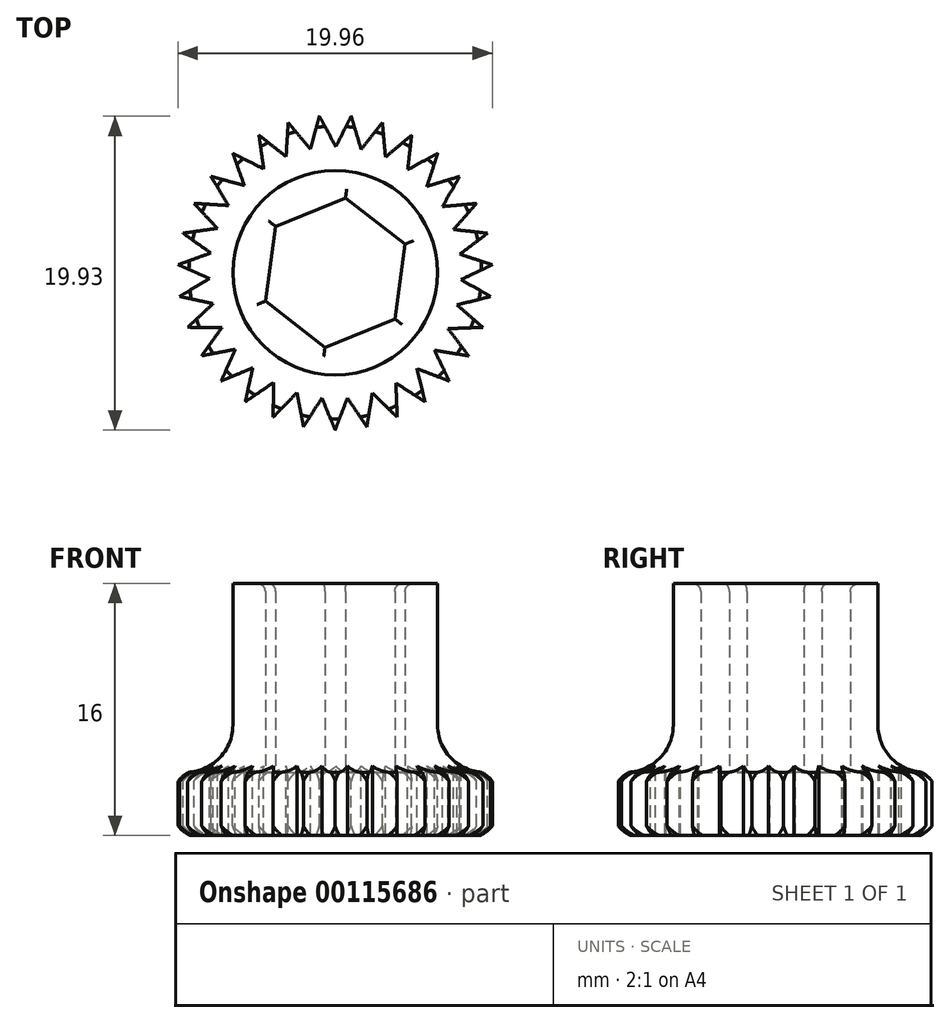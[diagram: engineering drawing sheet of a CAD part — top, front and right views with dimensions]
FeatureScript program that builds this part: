
annotation { "Feature Type Name" : "Feature", "Feature Type Description" : "" }
export const myFeature = defineFeature(function(context is Context, id is Id, definition is map)
    precondition{}
    {
        {
            var Q0;
            Q0=qCreatedBy(makeId("Top.planeOp"),FACE);
            var sketch = newSketch(context, id + "F0", { "sketchPlane" : qUnion([Q0])});
            skCircle(sketch, "E0.cCircle", {"center": v(0, 0) * mm, "radius": 4.15 * mm, "construction": true});
            skLineSegment(sketch, "E0.0", {"start": v(0.65, 4.75) * mm, "end": v(4.44, 1.81) * mm});
            skLineSegment(sketch, "E0.1", {"start": v(4.44, 1.81) * mm, "end": v(3.79, -2.94) * mm});
            skLineSegment(sketch, "E0.2", {"start": v(3.79, -2.94) * mm, "end": v(-0.65, -4.75) * mm});
            skLineSegment(sketch, "E0.3", {"start": v(-0.65, -4.75) * mm, "end": v(-4.44, -1.81) * mm});
            skLineSegment(sketch, "E0.4", {"start": v(-4.44, -1.81) * mm, "end": v(-3.79, 2.94) * mm});
            skLineSegment(sketch, "E0.5", {"start": v(-3.79, 2.94) * mm, "end": v(0.65, 4.75) * mm});
            skPoint(sketch, "E0.0.midPoint", {"position": v(2.54, 3.28) * mm});
            skCircle(sketch, "E1", {"center": v(0, 0) * mm, "radius": 6.5 * mm});
            skSolve(sketch);
        }
        {
            var Q0;
            Q0 = qSketchRegion(id + "F0", true);
            extrude(context, id + "F1", {"entities" : qUnion([Q0]), "depth" : 12 * mm});
        }
        {
            var Q0;
            Q0=makeQuery(id+"F1.opExtrude","CAP_FACE",FACE,{"disambiguationData":[OSD([sQuery(id+"F0.wireOp",EDGE,"E0.0"),sQuery(id+"F0.wireOp",EDGE,"E0.1"),sQuery(id+"F0.wireOp",EDGE,"E0.2"),sQuery(id+"F0.wireOp",EDGE,"E0.3"),sQuery(id+"F0.wireOp",EDGE,"E0.4"),sQuery(id+"F0.wireOp",EDGE,"E0.5"),sQuery(id+"F0.wireOp",EDGE,"E1")])],"isStart":true});
            var sketch = newSketch(context, id + "F2", { "sketchPlane" : qUnion([Q0])});
            skLineSegment(sketch, "E2", {"start": v(0, 0) * mm, "end": v(0, 8.68) * mm, "construction": true});
            skCircle(sketch, "E3", {"center": v(0, 0) * mm, "radius": 10 * mm, "construction": true});
            skCircle(sketch, "E4", {"center": v(0, 0) * mm, "radius": 8 * mm, "construction": true});
            skLineSegment(sketch, "E5", {"start": v(0, 10) * mm, "end": v(-0.85, 7.96) * mm});
            skLineSegment(sketch, "E6", {"start": v(-0.85, 7.96) * mm, "end": v(-2.02, 9.8) * mm});
            skLineSegment(sketch, "E7.1.0", {"start": v(-2.01, 9.8) * mm, "end": v(-2.43, 7.62) * mm});
            skLineSegment(sketch, "E7.1.1", {"start": v(-2.43, 7.62) * mm, "end": v(-3.95, 9.19) * mm});
            skLineSegment(sketch, "E7.2.0", {"start": v(-3.94, 9.19) * mm, "end": v(-3.92, 6.98) * mm});
            skLineSegment(sketch, "E7.2.1", {"start": v(-3.92, 6.98) * mm, "end": v(-5.72, 8.2) * mm});
            skLineSegment(sketch, "E7.3.0", {"start": v(-5.71, 8.2) * mm, "end": v(-5.24, 6.05) * mm});
            skLineSegment(sketch, "E7.3.1", {"start": v(-5.24, 6.05) * mm, "end": v(-7.25, 6.89) * mm});
            skLineSegment(sketch, "E7.4.0", {"start": v(-7.25, 6.89) * mm, "end": v(-6.35, 4.87) * mm});
            skLineSegment(sketch, "E7.4.1", {"start": v(-6.35, 4.87) * mm, "end": v(-8.49, 5.28) * mm});
            skLineSegment(sketch, "E7.5.0", {"start": v(-8.49, 5.29) * mm, "end": v(-7.2, 3.49) * mm});
            skLineSegment(sketch, "E7.5.1", {"start": v(-7.2, 3.49) * mm, "end": v(-9.38, 3.47) * mm});
            skLineSegment(sketch, "E7.6.0", {"start": v(-9.38, 3.47) * mm, "end": v(-7.75, 1.97) * mm});
            skLineSegment(sketch, "E7.6.1", {"start": v(-7.75, 1.97) * mm, "end": v(-9.89, 1.5) * mm});
            skLineSegment(sketch, "E7.7.0", {"start": v(-9.88, 1.51) * mm, "end": v(-8, 0.37) * mm});
            skLineSegment(sketch, "E7.7.1", {"start": v(-8, 0.37) * mm, "end": v(-9.99, -0.51) * mm});
            skLineSegment(sketch, "E7.8.0", {"start": v(-9.99, -0.5) * mm, "end": v(-7.9, -1.25) * mm});
            skLineSegment(sketch, "E7.8.1", {"start": v(-7.9, -1.25) * mm, "end": v(-9.68, -2.51) * mm});
            skLineSegment(sketch, "E7.9.0", {"start": v(-9.68, -2.5) * mm, "end": v(-7.49, -2.81) * mm});
            skLineSegment(sketch, "E7.9.1", {"start": v(-7.49, -2.81) * mm, "end": v(-8.98, -4.4) * mm});
            skLineSegment(sketch, "E7.10.0", {"start": v(-8.98, -4.4) * mm, "end": v(-6.77, -4.26) * mm});
            skLineSegment(sketch, "E7.10.1", {"start": v(-6.77, -4.26) * mm, "end": v(-7.9, -6.13) * mm});
            skLineSegment(sketch, "E7.11.0", {"start": v(-7.9, -6.12) * mm, "end": v(-5.77, -5.54) * mm});
            skLineSegment(sketch, "E7.11.1", {"start": v(-5.77, -5.54) * mm, "end": v(-6.5, -7.6) * mm});
            skLineSegment(sketch, "E7.12.0", {"start": v(-6.51, -7.59) * mm, "end": v(-4.54, -6.59) * mm});
            skLineSegment(sketch, "E7.12.1", {"start": v(-4.54, -6.59) * mm, "end": v(-4.85, -8.75) * mm});
            skLineSegment(sketch, "E7.13.0", {"start": v(-4.85, -8.74) * mm, "end": v(-3.12, -7.37) * mm});
            skLineSegment(sketch, "E7.13.1", {"start": v(-3.12, -7.37) * mm, "end": v(-2.99, -9.54) * mm});
            skLineSegment(sketch, "E7.14.0", {"start": v(-3, -9.54) * mm, "end": v(-1.57, -7.84) * mm});
            skLineSegment(sketch, "E7.14.1", {"start": v(-1.57, -7.84) * mm, "end": v(-1, -9.95) * mm});
            skLineSegment(sketch, "E7.15.0", {"start": v(-1.01, -9.95) * mm, "end": v(0.04, -8) * mm});
            skLineSegment(sketch, "E7.15.1", {"start": v(0.04, -8) * mm, "end": v(1.02, -9.95) * mm});
            skLineSegment(sketch, "E7.16.0", {"start": v(1.01, -9.95) * mm, "end": v(1.65, -7.83) * mm});
            skLineSegment(sketch, "E7.16.1", {"start": v(1.65, -7.83) * mm, "end": v(3, -9.54) * mm});
            skLineSegment(sketch, "E7.17.0", {"start": v(3, -9.54) * mm, "end": v(3.19, -7.34) * mm});
            skLineSegment(sketch, "E7.17.1", {"start": v(3.19, -7.34) * mm, "end": v(4.86, -8.74) * mm});
            skLineSegment(sketch, "E7.18.0", {"start": v(4.85, -8.74) * mm, "end": v(4.6, -6.54) * mm});
            skLineSegment(sketch, "E7.18.1", {"start": v(4.6, -6.54) * mm, "end": v(6.52, -7.58) * mm});
            skLineSegment(sketch, "E7.19.0", {"start": v(6.51, -7.59) * mm, "end": v(5.82, -5.48) * mm});
            skLineSegment(sketch, "E7.19.1", {"start": v(5.82, -5.48) * mm, "end": v(7.91, -6.12) * mm});
            skLineSegment(sketch, "E7.20.0", {"start": v(7.9, -6.12) * mm, "end": v(6.8, -4.2) * mm});
            skLineSegment(sketch, "E7.20.1", {"start": v(6.8, -4.2) * mm, "end": v(8.98, -4.4) * mm});
            skLineSegment(sketch, "E7.21.0", {"start": v(8.98, -4.4) * mm, "end": v(7.52, -2.74) * mm});
            skLineSegment(sketch, "E7.21.1", {"start": v(7.52, -2.74) * mm, "end": v(9.68, -2.5) * mm});
            skLineSegment(sketch, "E7.22.0", {"start": v(9.68, -2.5) * mm, "end": v(7.91, -1.17) * mm});
            skLineSegment(sketch, "E7.22.1", {"start": v(7.91, -1.17) * mm, "end": v(9.99, -0.5) * mm});
            skLineSegment(sketch, "E7.23.0", {"start": v(9.99, -0.5) * mm, "end": v(7.99, 0.44) * mm});
            skLineSegment(sketch, "E7.23.1", {"start": v(7.99, 0.44) * mm, "end": v(9.88, 1.52) * mm});
            skLineSegment(sketch, "E7.24.0", {"start": v(9.88, 1.51) * mm, "end": v(7.74, 2.04) * mm});
            skLineSegment(sketch, "E7.24.1", {"start": v(7.74, 2.04) * mm, "end": v(9.38, 3.48) * mm});
            skLineSegment(sketch, "E8.2.25.0", {"start": v(9.38, 3.47) * mm, "end": v(7.17, 3.56) * mm});
            skLineSegment(sketch, "E8.3.25.0", {"start": v(7.17, 3.56) * mm, "end": v(8.48, 5.3) * mm});
            skLineSegment(sketch, "E9.2.26.0", {"start": v(8.49, 5.29) * mm, "end": v(6.3, 4.93) * mm});
            skLineSegment(sketch, "E9.3.26.0", {"start": v(6.3, 4.93) * mm, "end": v(7.24, 6.9) * mm});
            skLineSegment(sketch, "E9.2.27.0", {"start": v(7.25, 6.89) * mm, "end": v(5.18, 6.1) * mm});
            skLineSegment(sketch, "E9.3.27.0", {"start": v(5.18, 6.1) * mm, "end": v(5.7, 8.21) * mm});
            skLineSegment(sketch, "E9.2.28.0", {"start": v(5.71, 8.2) * mm, "end": v(3.85, 7.01) * mm});
            skLineSegment(sketch, "E9.3.28.0", {"start": v(3.85, 7.01) * mm, "end": v(3.94, 9.2) * mm});
            skLineSegment(sketch, "E10.2.29.0", {"start": v(3.94, 9.19) * mm, "end": v(2.36, 7.64) * mm});
            skLineSegment(sketch, "E10.3.29.0", {"start": v(2.36, 7.64) * mm, "end": v(2, 9.8) * mm});
            skLineSegment(sketch, "E10.2.30.0", {"start": v(2.01, 9.8) * mm, "end": v(0.77, 7.96) * mm});
            skLineSegment(sketch, "E10.3.30.0", {"start": v(0.77, 7.96) * mm, "end": v(0, 10) * mm});
            skSolve(sketch);
        }
        {
            var Q0;
            Q0 = qSketchRegion(id + "F2", true);
            extrude(context, id + "F3", {"entities" : qUnion([Q0]), "operationType" : NewBodyOperationType.ADD, "depth" : 4 * mm});
        }
        {
            var Q0;
            Q0=makeQuery(id+"F1.opExtrude","CAP_EDGE",EDGE,{"disambiguationData":[OSD([sQuery(id+"F0.wireOp",EDGE,"E1")])],"isStart":true});
            fillet(context, id + "F4", {"entities" : qUnion([Q0]), "radius" : 3 * mm, "tangentPropagation" : true, "allowEdgeOverflow" : false});
        }
        {
            var Q0;
            Q0=qCreatedBy(makeId("Right.planeOp"),FACE);
            var sketch = newSketch(context, id + "F5", { "sketchPlane" : qUnion([Q0])});
            skPoint(sketch, "E11.0", {"position": v(2.5, -4) * mm});
            skLineSegment(sketch, "E12", {"start": v(0, -4) * mm, "end": v(-4.72, -4) * mm});
            skLineSegment(sketch, "E13", {"start": v(-10, -4) * mm, "end": v(-10, 0.3) * mm});
            skLineSegment(sketch, "E14", {"start": v(-10, 0.3) * mm, "end": v(-12.39, -5.28) * mm});
            skLineSegment(sketch, "E15", {"start": v(-12.39, -5.28) * mm, "end": v(0, -4.92) * mm});
            skArc(sketch, "E16", {"start": v(-8.86, 0.19) * mm, "mid": v(-10.44, -2.42) * mm, "end": v(-7.99, -4.23) * mm});
            skLineSegment(sketch, "E17", {"start": v(-7.99, -4.23) * mm, "end": v(-4.72, -4) * mm});
            skLineSegment(sketch, "E18", {"start": v(-8.86, 0.19) * mm, "end": v(-10, 0.3) * mm});
            skLineSegment(sketch, "E19.trimOffspring", {"start": v(-9.24, -4) * mm, "end": v(-10, -4) * mm});
            skLineSegment(sketch, "E20", {"start": v(0, -5.6) * mm, "end": v(0, 3.11) * mm, "construction": true});
            skLineSegment(sketch, "E21", {"start": v(0, -4.92) * mm, "end": v(0, -4) * mm});
            skSolve(sketch);
        }
        {
            var Q0;
            Q0 = qSketchRegion(id + "F5", true);
            var Q1;
            Q1=sQuery(id+"F5.wireOp",EDGE,"E20");
            revolve(context, id + "F6", {"operationType" : NewBodyOperationType.REMOVE, "entities" : qUnion([Q0]), "axis" : qUnion([Q1]), "revolveType" : RevolveType.FULL, "oppositeDirection" : true});
        }
        {
            var Q0;
            Q0=makeQuery(id+"F1.opExtrude","CAP_EDGE",EDGE,{"disambiguationData":[OSD([sQuery(id+"F0.wireOp",EDGE,"E0.1")])],"isStart":false});
            var Q1;
            Q1=makeQuery(id+"F1.opExtrude","CAP_EDGE",EDGE,{"disambiguationData":[OSD([sQuery(id+"F0.wireOp",EDGE,"E0.0")])],"isStart":false});
            var Q2;
            Q2=makeQuery(id+"F1.opExtrude","CAP_EDGE",EDGE,{"disambiguationData":[OSD([sQuery(id+"F0.wireOp",EDGE,"E0.5")])],"isStart":false});
            var Q3;
            Q3=makeQuery(id+"F1.opExtrude","CAP_EDGE",EDGE,{"disambiguationData":[OSD([sQuery(id+"F0.wireOp",EDGE,"E0.4")])],"isStart":false});
            var Q4;
            Q4=makeQuery(id+"F1.opExtrude","CAP_EDGE",EDGE,{"disambiguationData":[OSD([sQuery(id+"F0.wireOp",EDGE,"E0.3")])],"isStart":false});
            var Q5;
            Q5=makeQuery(id+"F1.opExtrude","CAP_EDGE",EDGE,{"disambiguationData":[OSD([sQuery(id+"F0.wireOp",EDGE,"E0.2")])],"isStart":false});
            fillet(context, id + "F7", {"entities" : qUnion([Q0, Q1, Q2, Q3, Q4, Q5]), "radius" : 0.5 * mm, "tangentPropagation" : true, "allowEdgeOverflow" : false});
        }
    });
